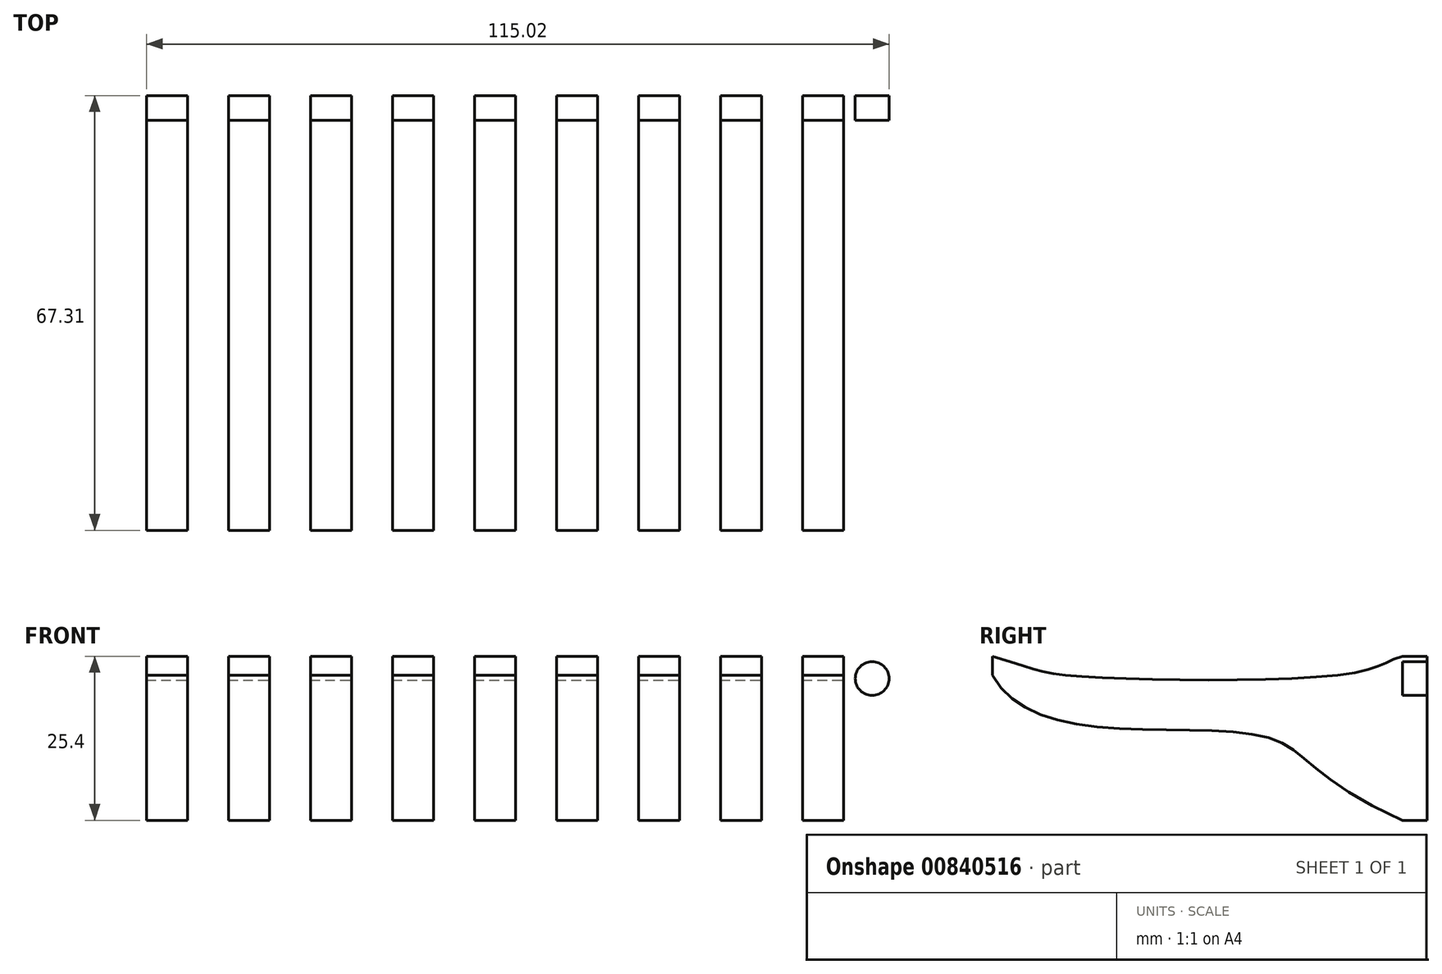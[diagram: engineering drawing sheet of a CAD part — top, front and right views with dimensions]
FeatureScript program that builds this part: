
annotation { "Feature Type Name" : "Feature", "Feature Type Description" : "" }
export const myFeature = defineFeature(function(context is Context, id is Id, definition is map)
    precondition{}
    {
        {
            var Q0;
            Q0=qCreatedBy(makeId("Front.planeOp"),FACE);
            var sketch = newSketch(context, id + "F0", { "sketchPlane" : qUnion([Q0])});
            skLineSegment(sketch, "E0.bottom", {"start": v(63.5, -19.05) * mm, "end": v(-63.5, -19.05) * mm});
            skLineSegment(sketch, "E0.top", {"start": v(63.5, 19.05) * mm, "end": v(-63.5, 19.05) * mm});
            skLineSegment(sketch, "E0.left", {"start": v(63.5, -19.05) * mm, "end": v(63.5, 19.05) * mm});
            skLineSegment(sketch, "E0.right", {"start": v(-63.5, -19.05) * mm, "end": v(-63.5, 19.05) * mm});
            skPoint(sketch, "E0.middle", {"position": v(0, 0) * mm});
            skSolve(sketch);
        }
        {
            var Q0;
            Q0=makeQuery(id+"F0.imprint","IMPRINT",FACE,{"disambiguationData":[TD([[makeQuery(id+"F0.imprint","IMPRINT",EDGE,{"derivedFrom":sQuery(id+"F0.wireOp",EDGE,"E0.bottom")}),-1.0]])]});
            extrude(context, id + "F1", {"entities" : qUnion([Q0]), "depth" : 3.8 * mm, "offsetDistance" : 25.4 * mm});
        }
        {
            var Q0;
            Q0=makeQuery(id+"F1.opExtrude","CAP_FACE",FACE,{"disambiguationData":[OSD([sQuery(id+"F0.wireOp",EDGE,"E0.bottom"),sQuery(id+"F0.wireOp",EDGE,"E0.top"),sQuery(id+"F0.wireOp",EDGE,"E0.left"),sQuery(id+"F0.wireOp",EDGE,"E0.right")])],"isStart":false});
            var sketch = newSketch(context, id + "F2", { "sketchPlane" : qUnion([Q0])});
            skLineSegment(sketch, "E1.bottom", {"start": v(3.18, 12.7) * mm, "end": v(-3.18, 12.7) * mm});
            skLineSegment(sketch, "E1.top", {"start": v(3.17, -12.7) * mm, "end": v(-3.18, -12.7) * mm});
            skLineSegment(sketch, "E1.left", {"start": v(3.18, 12.7) * mm, "end": v(3.17, -12.7) * mm});
            skLineSegment(sketch, "E1.right", {"start": v(-3.18, 12.7) * mm, "end": v(-3.18, -12.7) * mm});
            skPoint(sketch, "E1.middle", {"position": v(0, 0) * mm});
            skLineSegment(sketch, "E2.1.0.0", {"start": v(-9.53, 12.7) * mm, "end": v(-9.53, -12.7) * mm});
            skLineSegment(sketch, "E2.1.0.1", {"start": v(-9.53, 12.7) * mm, "end": v(-15.88, 12.7) * mm});
            skLineSegment(sketch, "E2.1.0.2", {"start": v(-15.88, 12.7) * mm, "end": v(-15.88, -12.7) * mm});
            skLineSegment(sketch, "E2.1.0.3", {"start": v(-9.52, -12.7) * mm, "end": v(-15.88, -12.7) * mm});
            skLineSegment(sketch, "E2.2.0.0", {"start": v(-22.23, 12.7) * mm, "end": v(-22.23, -12.7) * mm});
            skLineSegment(sketch, "E2.2.0.1", {"start": v(-22.23, 12.7) * mm, "end": v(-28.58, 12.7) * mm});
            skLineSegment(sketch, "E2.2.0.2", {"start": v(-28.58, 12.7) * mm, "end": v(-28.58, -12.7) * mm});
            skLineSegment(sketch, "E2.2.0.3", {"start": v(-22.23, -12.7) * mm, "end": v(-28.58, -12.7) * mm});
            skLineSegment(sketch, "E3.0.3.0", {"start": v(-34.93, 12.7) * mm, "end": v(-34.93, -12.7) * mm});
            skLineSegment(sketch, "E3.3.3.0", {"start": v(-34.93, 12.7) * mm, "end": v(-41.28, 12.7) * mm});
            skLineSegment(sketch, "E3.6.3.0", {"start": v(-41.28, 12.7) * mm, "end": v(-41.28, -12.7) * mm});
            skLineSegment(sketch, "E3.9.3.0", {"start": v(-34.93, -12.7) * mm, "end": v(-41.28, -12.7) * mm});
            skLineSegment(sketch, "E3.0.4.0", {"start": v(-47.63, 12.7) * mm, "end": v(-47.63, -12.7) * mm});
            skLineSegment(sketch, "E3.3.4.0", {"start": v(-47.62, 12.7) * mm, "end": v(-53.97, 12.7) * mm});
            skLineSegment(sketch, "E3.6.4.0", {"start": v(-53.98, 12.7) * mm, "end": v(-53.98, -12.7) * mm});
            skLineSegment(sketch, "E3.9.4.0", {"start": v(-47.62, -12.7) * mm, "end": v(-53.98, -12.7) * mm});
            skLineSegment(sketch, "E4.1.0.0", {"start": v(15.88, 12.7) * mm, "end": v(15.88, -12.7) * mm});
            skLineSegment(sketch, "E4.1.0.1", {"start": v(15.88, 12.7) * mm, "end": v(9.53, 12.7) * mm});
            skLineSegment(sketch, "E4.1.0.2", {"start": v(9.53, 12.7) * mm, "end": v(9.53, -12.7) * mm});
            skLineSegment(sketch, "E4.2.0.0", {"start": v(28.58, 12.7) * mm, "end": v(28.58, -12.7) * mm});
            skLineSegment(sketch, "E4.2.0.1", {"start": v(28.58, 12.7) * mm, "end": v(22.23, 12.7) * mm});
            skLineSegment(sketch, "E4.2.0.2", {"start": v(22.23, 12.7) * mm, "end": v(22.23, -12.7) * mm});
            skLineSegment(sketch, "E4.3.0.0", {"start": v(41.27, 12.7) * mm, "end": v(41.27, -12.7) * mm});
            skLineSegment(sketch, "E4.3.0.1", {"start": v(41.28, 12.7) * mm, "end": v(34.93, 12.7) * mm});
            skLineSegment(sketch, "E4.3.0.2", {"start": v(34.92, 12.7) * mm, "end": v(34.92, -12.7) * mm});
            skLineSegment(sketch, "E4.4.0.0", {"start": v(53.98, 12.7) * mm, "end": v(53.98, -12.7) * mm});
            skLineSegment(sketch, "E4.4.0.1", {"start": v(53.98, 12.7) * mm, "end": v(47.63, 12.7) * mm});
            skLineSegment(sketch, "E4.4.0.2", {"start": v(47.62, 12.7) * mm, "end": v(47.62, -12.7) * mm});
            skLineSegment(sketch, "E5", {"start": v(9.53, -12.7) * mm, "end": v(15.88, -12.7) * mm});
            skLineSegment(sketch, "E6", {"start": v(22.23, -12.7) * mm, "end": v(28.58, -12.7) * mm});
            skLineSegment(sketch, "E7", {"start": v(34.92, -12.7) * mm, "end": v(41.27, -12.7) * mm});
            skLineSegment(sketch, "E8", {"start": v(47.62, -12.7) * mm, "end": v(53.98, -12.7) * mm});
            skSolve(sketch);
        }
        {
            var Q0;
            Q0=makeQuery(id+"F2.imprint","IMPRINT",FACE,{"disambiguationData":[TD([[makeQuery(id+"F2.imprint","IMPRINT",EDGE,{"derivedFrom":sQuery(id+"F2.wireOp",EDGE,"E1.bottom")}),1.0]])]});
            var Q1;
            Q1=makeQuery(id+"F2.imprint","IMPRINT",FACE,{"disambiguationData":[TD([[makeQuery(id+"F2.imprint","IMPRINT",EDGE,{"derivedFrom":sQuery(id+"F2.wireOp",EDGE,"E2.1.0.0")}),-1.0]])]});
            var Q2;
            Q2=makeQuery(id+"F2.imprint","IMPRINT",FACE,{"disambiguationData":[TD([[makeQuery(id+"F2.imprint","IMPRINT",EDGE,{"derivedFrom":sQuery(id+"F2.wireOp",EDGE,"E2.2.0.0")}),-1.0]])]});
            var Q3;
            Q3=makeQuery(id+"F2.imprint","IMPRINT",FACE,{"disambiguationData":[TD([[makeQuery(id+"F2.imprint","IMPRINT",EDGE,{"derivedFrom":sQuery(id+"F2.wireOp",EDGE,"E3.0.3.0")}),-1.0]])]});
            var Q4;
            Q4=makeQuery(id+"F2.imprint","IMPRINT",FACE,{"disambiguationData":[TD([[makeQuery(id+"F2.imprint","IMPRINT",EDGE,{"derivedFrom":sQuery(id+"F2.wireOp",EDGE,"E3.0.4.0")}),-1.0]])]});
            var Q5;
            Q5=makeQuery(id+"F2.imprint","IMPRINT",FACE,{"disambiguationData":[TD([[makeQuery(id+"F2.imprint","IMPRINT",EDGE,{"derivedFrom":sQuery(id+"F2.wireOp",EDGE,"E4.1.0.0")}),-1.0]])]});
            var Q6;
            Q6=makeQuery(id+"F2.imprint","IMPRINT",FACE,{"disambiguationData":[TD([[makeQuery(id+"F2.imprint","IMPRINT",EDGE,{"derivedFrom":sQuery(id+"F2.wireOp",EDGE,"E4.2.0.0")}),-1.0]])]});
            var Q7;
            Q7=makeQuery(id+"F2.imprint","IMPRINT",FACE,{"disambiguationData":[TD([[makeQuery(id+"F2.imprint","IMPRINT",EDGE,{"derivedFrom":sQuery(id+"F2.wireOp",EDGE,"E4.3.0.0")}),-1.0]])]});
            var Q8;
            Q8=makeQuery(id+"F2.imprint","IMPRINT",FACE,{"disambiguationData":[TD([[makeQuery(id+"F2.imprint","IMPRINT",EDGE,{"derivedFrom":sQuery(id+"F2.wireOp",EDGE,"E4.4.0.0")}),-1.0]])]});
            extrude(context, id + "F3", {"entities" : qUnion([Q0, Q1, Q2, Q3, Q4, Q5, Q6, Q7, Q8]), "operationType" : NewBodyOperationType.ADD, "depth" : 63.5 * mm, "offsetDistance" : 25.4 * mm});
        }
        {
            var Q0;
            Q0=makeQuery(id+"F3.opExtrude","SWEPT_FACE",FACE,{"disambiguationData":[OSD([sQuery(id+"F2.wireOp",EDGE,"E1.right")])]});
            var sketch = newSketch(context, id + "F4", { "sketchPlane" : qUnion([Q0])});
            skFitSpline(sketch, "E9", {"points": [v(3.81, -12.7) * mm, v(24.31, 0) * mm, v(52.46, 1.9) * mm, v(67.3, 9.76) * mm], "startDerivative": vector(121.9, 53.98) * mm, "endDerivative": vector(27.46, 48.71) * mm});
            skFitSpline(sketch, "E10", {"points": [v(3.81, 12.7) * mm, v(10.84, 10.22) * mm, v(55.48, 9.73) * mm, v(67.3, 12.7) * mm], "startDerivative": vector(35.37, -10.38) * mm, "endDerivative": vector(72.8, 21.18) * mm});
            skSolve(sketch);
        }
        {
            var Q0;
            Q0=makeQuery(id+"F4.imprint","IMPRINT",FACE,{"disambiguationData":[TD([[makeQuery(id+"F4.imprint","IMPRINT",EDGE,{"derivedFrom":sQuery(id+"F4.wireOp",EDGE,"E10")}),1.0]])]});
            var Q1;
            {var subQ0=sQuery(id+"F4.wireOp",EDGE,"E9");Q1=makeQuery(id+"F4.imprint","IMPRINT",FACE,{"disambiguationData":[TD([[makeQuery(id+"F4.imprint","IMPRINT",EDGE,{"derivedFrom":subQ0}),-1.0]])]});}
            extrude(context, id + "F5", {"entities" : qUnion([Q0, Q1]), "operationType" : NewBodyOperationType.REMOVE, "endBound" : BoundingType.SYMMETRIC, "oppositeDirection" : true, "depth" : 127 * mm, "offsetDistance" : 25.4 * mm});
        }
        {
            var Q0;
            Q0=makeQuery(id+"F1.opExtrude","CAP_FACE",FACE,{"disambiguationData":[OSD([sQuery(id+"F0.wireOp",EDGE,"E0.bottom"),sQuery(id+"F0.wireOp",EDGE,"E0.top"),sQuery(id+"F0.wireOp",EDGE,"E0.left"),sQuery(id+"F0.wireOp",EDGE,"E0.right")])],"isStart":false});
            var sketch = newSketch(context, id + "F6", { "sketchPlane" : qUnion([Q0])});
            skCircle(sketch, "E11", {"center": v(-58.42, 9.25) * mm, "radius": 2.62 * mm});
            skCircle(sketch, "E12.MirrorC", {"center": v(58.42, 9.25) * mm, "radius": 2.62 * mm});
            skSolve(sketch);
        }
        {
            var Q0;
            Q0=makeQuery(id+"F6.imprint","IMPRINT",FACE,{"disambiguationData":[TD([[makeQuery(id+"F6.imprint","IMPRINT",EDGE,{"derivedFrom":sQuery(id+"F6.wireOp",EDGE,"E11")}),1.0]])]});
            var Q1;
            Q1=makeQuery(id+"F6.imprint","IMPRINT",FACE,{"disambiguationData":[TD([[makeQuery(id+"F6.imprint","IMPRINT",EDGE,{"derivedFrom":sQuery(id+"F6.wireOp",EDGE,"E12.MirrorC")}),-1.0]])]});
            extrude(context, id + "F7", {"entities" : qUnion([Q0, Q1]), "operationType" : NewBodyOperationType.REMOVE, "endBound" : BoundingType.THROUGH_ALL, "oppositeDirection" : true, "depth" : 25.4 * mm, "offsetDistance" : 25.4 * mm});
        }
    });
